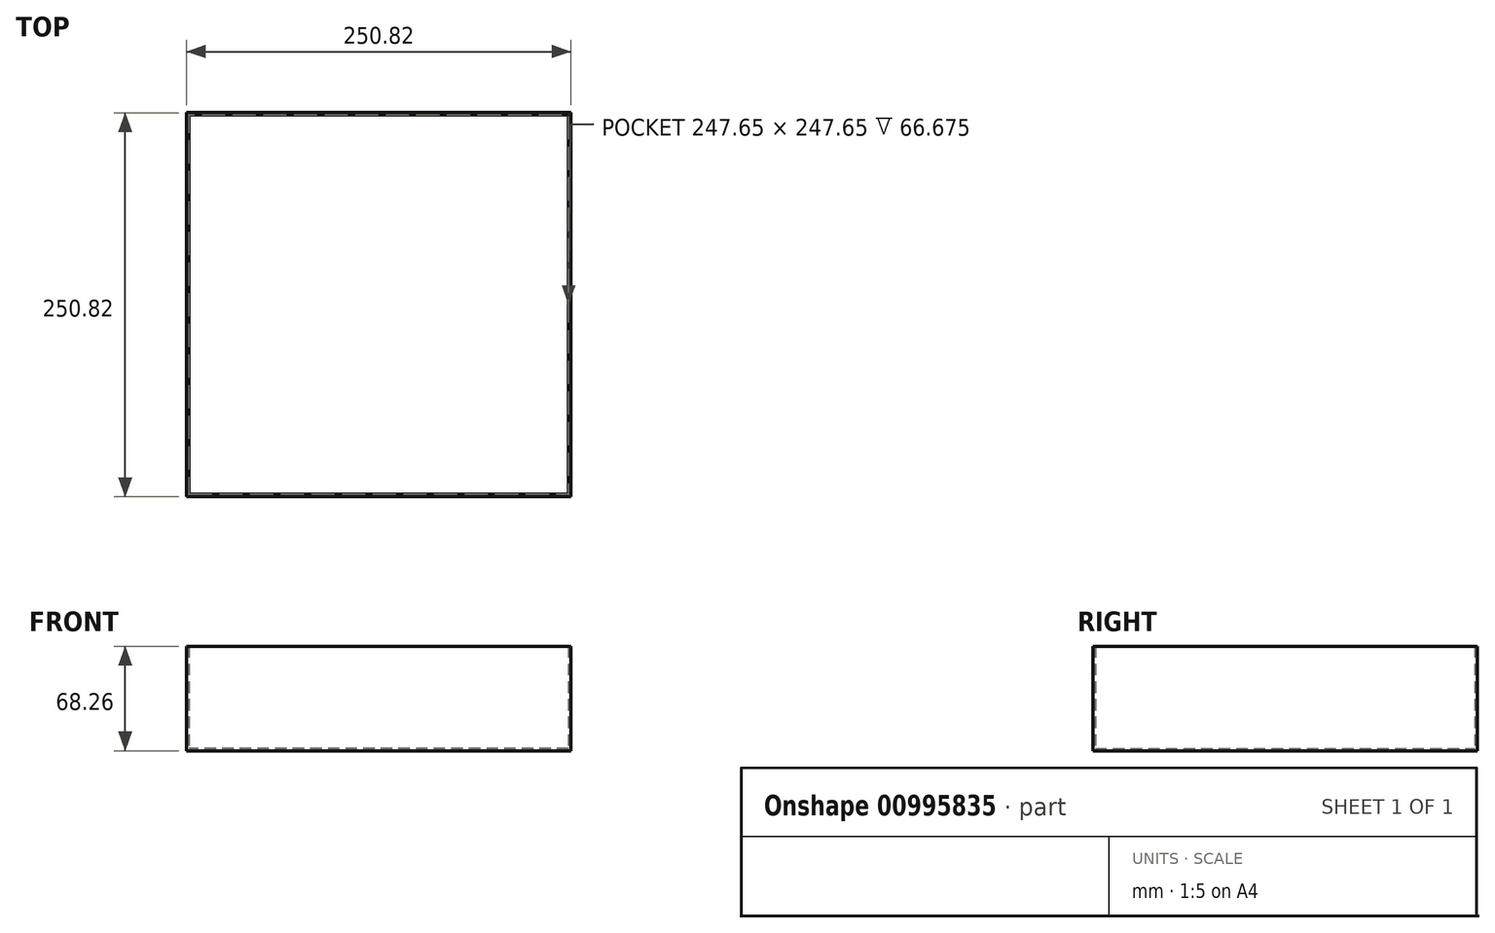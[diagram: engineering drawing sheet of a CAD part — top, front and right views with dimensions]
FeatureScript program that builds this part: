
annotation { "Feature Type Name" : "Feature", "Feature Type Description" : "" }
export const myFeature = defineFeature(function(context is Context, id is Id, definition is map)
    precondition{}
    {
        {
            var Q0;
            Q0=qCreatedBy(makeId("Top.planeOp"),FACE);
            var sketch = newSketch(context, id + "F0", { "sketchPlane" : qUnion([Q0])});
            skLineSegment(sketch, "E0.bottom", {"start": v(123.83, -123.83) * mm, "end": v(-123.83, -123.83) * mm});
            skLineSegment(sketch, "E0.top", {"start": v(123.83, 123.83) * mm, "end": v(-123.83, 123.83) * mm});
            skLineSegment(sketch, "E0.left", {"start": v(123.83, -123.83) * mm, "end": v(123.83, 123.83) * mm});
            skLineSegment(sketch, "E0.right", {"start": v(-123.83, -123.83) * mm, "end": v(-123.83, 123.83) * mm});
            skPoint(sketch, "E0.middle", {"position": v(0, 0) * mm});
            skSolve(sketch);
        }
        {
            var Q0;
            Q0 = qSketchRegion(id + "F0", true);
            extrude(context, id + "F1", {"entities" : qUnion([Q0]), "depth" : 1.59 * mm, "offsetDistance" : 25.4 * mm});
        }
        {
            var Q0;
            Q0=qCreatedBy(makeId("Top.planeOp"),FACE);
            var sketch = newSketch(context, id + "F2", { "sketchPlane" : qUnion([Q0])});
            skLineSegment(sketch, "E1.bottom", {"start": v(-125.41, -125.41) * mm, "end": v(125.41, -125.41) * mm});
            skLineSegment(sketch, "E1.top", {"start": v(-125.41, 125.41) * mm, "end": v(125.41, 125.41) * mm});
            skLineSegment(sketch, "E1.left", {"start": v(-125.41, -125.41) * mm, "end": v(-125.41, 125.41) * mm});
            skLineSegment(sketch, "E1.right", {"start": v(125.41, -125.41) * mm, "end": v(125.41, 125.41) * mm});
            skPoint(sketch, "E1.middle", {"position": v(0, 0) * mm});
            skLineSegment(sketch, "E2.0.0", {"start": v(123.83, -123.83) * mm, "end": v(123.82, 123.83) * mm});
            skLineSegment(sketch, "E2.0.1", {"start": v(123.82, 123.83) * mm, "end": v(-123.83, 123.83) * mm});
            skLineSegment(sketch, "E2.0.2", {"start": v(-123.83, 123.83) * mm, "end": v(-123.83, -123.83) * mm});
            skLineSegment(sketch, "E2.0.3", {"start": v(-123.83, -123.83) * mm, "end": v(123.83, -123.83) * mm});
            skSolve(sketch);
        }
        {
            var Q0;
            Q0 = qSketchRegion(id + "F2", true);
            extrude(context, id + "F3", {"entities" : qUnion([Q0]), "operationType" : NewBodyOperationType.ADD, "depth" : 68.26 * mm, "offsetDistance" : 25.4 * mm});
        }
    });
